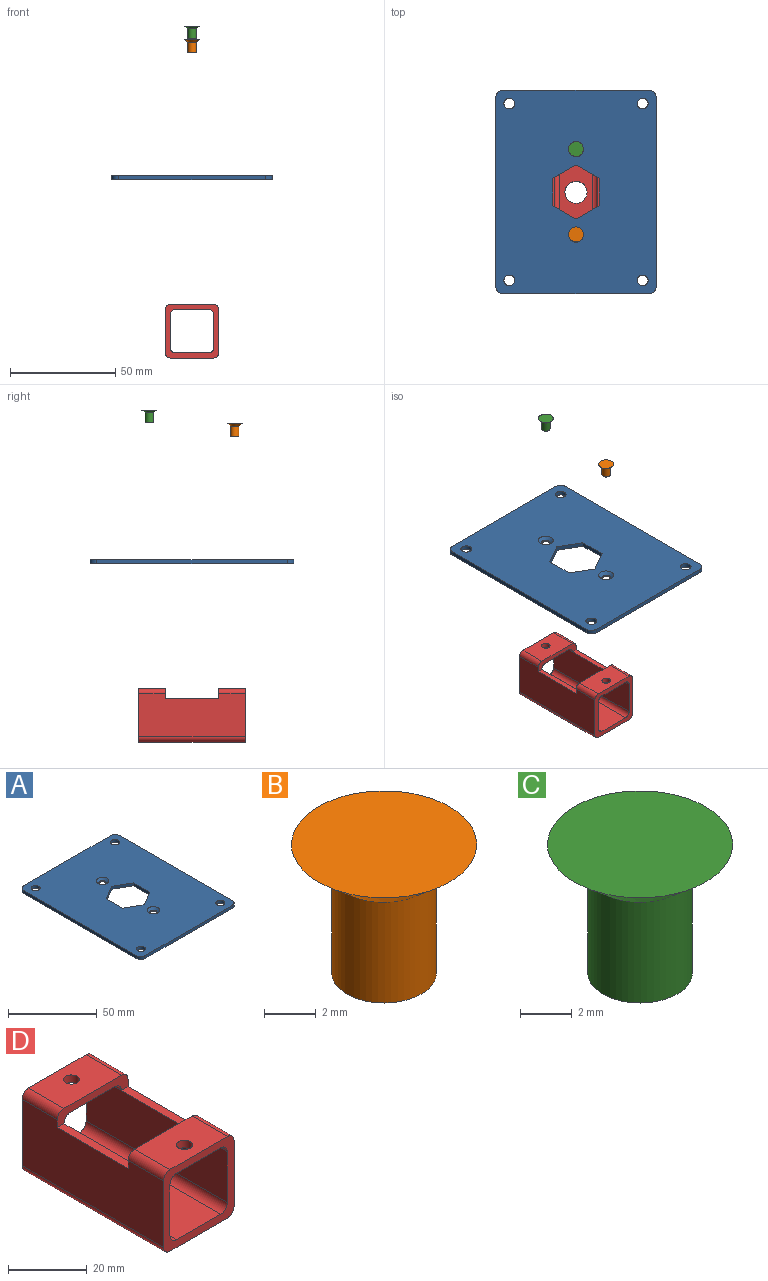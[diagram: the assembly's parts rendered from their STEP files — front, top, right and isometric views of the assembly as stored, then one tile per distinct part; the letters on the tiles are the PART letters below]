
ASSEMBLY  parts=4 mates=3
PART A: 24 faces, bbox 76.2x96.8x2 mm
  f0: plane 11.11x6.42mm, normal (0.5,-0.87,0), area 26.1mm2, adj f1,f13,f14,f15
  f1: plane 11.11x6.42mm, normal (-0.5,-0.87,0), area 26.1mm2, adj f0,f2,f14,f15
  f2: plane 12.83x2.03mm, normal (-1,0,0), area 26.1mm2, adj f1,f3,f14,f15
  f3: plane 11.11x6.42mm, normal (-0.5,0.87,0), area 26.1mm2, adj f2,f4,f14,f15
  f4: plane 11.11x6.42mm, normal (0.5,0.87,0), area 26.1mm2, adj f3,f13,f14,f15
  f5: plane 90.49x2.03mm, normal (1,0,0), area 183.9mm2, adj f6,f12,f14,f15
  f6: cylinder r=3.17mm len=3.18mm, axis (0,0,-1), area 10.1mm2, adj f5,f7,f14,f15
  f7: plane 69.85x2.03mm, normal (0,1,0), area 141.9mm2, adj f6,f8,f14,f15
  f8: cylinder r=3.17mm len=3.18mm, axis (0,0,-1), area 10.1mm2, adj f7,f9,f14,f15
  f9: plane 90.49x2.03mm, normal (-1,0,0), area 183.9mm2, adj f8,f10,f14,f15
  f10: cylinder r=3.17mm len=3.18mm, axis (0,0,-1), area 10.1mm2, adj f9,f11,f14,f15
  f11: plane 69.85x2.03mm, normal (0,-1,0), area 141.9mm2, adj f10,f12,f14,f15
  f12: cylinder r=3.17mm len=3.18mm, axis (0,0,-1), area 10.1mm2, adj f5,f11,f14,f15
  f13: plane 12.83x2.03mm, normal (1,0,0), area 26.1mm2, adj f0,f4,f14,f15
  f14: plane 96.84x76.2mm, normal (0,0,1), area 6780.5mm2, adj f0,f1,f2,f3,f4,f5,f6,f7
  f15: plane 96.84x76.2mm, normal (0,0,-1), area 6835.1mm2, adj f0,f1,f2,f3,f4,f5,f6,f7
  f16: cylinder r=2.55mm len=5.11mm, axis (0,0,-1), area 32.6mm2, adj f14,f15
  f17: cylinder r=2.55mm len=5.11mm, axis (0,0,-1), area 32.6mm2, adj f14,f15
  f18: cylinder r=2.55mm len=5.11mm, axis (0,0,-1), area 32.6mm2, adj f14,f15
  f19: cylinder r=2.55mm len=5.11mm, axis (0,0,-1), area 32.6mm2, adj f14,f15
  f20: cylinder r=2.02mm len=4.04mm, axis (0,0,1), area 9.3mm2, adj f15,f21
  f21: cone r=2.02mm half-angle=50deg, axis (0,0,1), area 35.6mm2, adj f14,f20
  f22: cylinder r=2.02mm len=4.04mm, axis (0,0,1), area 9.3mm2, adj f15,f23
  f23: cone r=2.02mm half-angle=50deg, axis (0,0,1), area 35.6mm2, adj f14,f22
PART B: 4 faces, bbox 7.1x7.1x6.1 mm
  f0: plane 7.14x7.14mm, normal (0,0,1), area 40.1mm2, adj f1
  f1: cone r=3.57mm half-angle=50deg, axis (0,0,1), area 35.6mm2, adj f0,f2
  f2: cylinder r=2.02mm len=4.76mm, axis (0,0,1), area 60.4mm2, adj f1,f3
  f3: plane 4.04x4.04mm, normal (0,0,-1), area 12.8mm2, adj f2
PART C: 4 faces, bbox 7.1x7.1x6.1 mm
  f0: plane 7.14x7.14mm, normal (0,0,1), area 40.1mm2, adj f1
  f1: cone r=3.57mm half-angle=50deg, axis (0,0,1), area 35.6mm2, adj f0,f2
  f2: cylinder r=2.02mm len=4.76mm, axis (0,0,1), area 60.4mm2, adj f1,f3
  f3: plane 4.04x4.04mm, normal (0,0,-1), area 12.8mm2, adj f2
PART D: 31 faces, bbox 25.4x50.8x25.4 mm
  f0: plane 20.64x12.7mm, normal (0,0,1), area 249.3mm2, adj f7,f9,f23,f25,f26
  f1: cylinder r=2.38mm len=12.7mm, axis (0,1,0), area 47.5mm2, adj f6,f8,f22,f27
  f2: cylinder r=2.38mm len=12.7mm, axis (0,1,0), area 47.5mm2, adj f8,f10,f22,f27
  f3: cylinder r=2.38mm len=12.7mm, axis (0,1,0), area 47.5mm2, adj f4,f17,f22,f27
  f4: plane 15.88x12.7mm, normal (0,0,-1), area 188.8mm2, adj f3,f5,f22,f24,f27
  f5: cylinder r=2.38mm len=12.7mm, axis (0,1,0), area 47.5mm2, adj f4,f21,f22,f27
  f6: plane 50.8x20.64mm, normal (1,0,0), area 987.9mm2, adj f1,f7,f13,f22,f23,f26,f27,f28
  f7: cylinder r=2.38mm len=12.7mm, axis (0,1,0), area 47.5mm2, adj f0,f6,f23,f26
  f8: plane 20.64x12.7mm, normal (0,0,1), area 249.3mm2, adj f1,f2,f22,f24,f27
  f9: cylinder r=2.38mm len=12.7mm, axis (0,1,0), area 47.5mm2, adj f0,f10,f23,f26
  f10: plane 50.8x20.64mm, normal (-1,0,0), area 987.9mm2, adj f2,f9,f11,f22,f23,f26,f27,f29
  f11: cylinder r=2.38mm len=50.8mm, axis (0,1,0), area 190mm2, adj f10,f12,f22,f23
  f12: plane 50.8x20.64mm, normal (0,0,-1), area 962mm2, adj f11,f13,f22,f23,f30
  f13: cylinder r=2.38mm len=50.8mm, axis (0,1,0), area 190mm2, adj f6,f12,f22,f23
  f14: cylinder r=2.38mm len=50.8mm, axis (0,1,0), area 190mm2, adj f15,f21,f22,f23
  f15: plane 50.8x15.88mm, normal (0,0,1), area 720mm2, adj f14,f16,f22,f23,f30
  f16: cylinder r=2.38mm len=50.8mm, axis (0,1,0), area 190mm2, adj f15,f17,f22,f23
  f17: plane 50.8x15.88mm, normal (1,0,0), area 806.5mm2, adj f3,f16,f18,f22,f23,f29
  f18: cylinder r=2.38mm len=12.7mm, axis (0,1,0), area 47.5mm2, adj f17,f19,f23,f26
  f19: plane 15.88x12.7mm, normal (0,0,-1), area 188.8mm2, adj f18,f20,f23,f25,f26
  f20: cylinder r=2.38mm len=12.7mm, axis (0,1,0), area 47.5mm2, adj f19,f21,f23,f26
  f21: plane 50.8x15.88mm, normal (-1,0,0), area 806.5mm2, adj f5,f14,f20,f22,f23,f28
  f22: plane 25.4x25.4mm, normal (0,-1,0), area 219.3mm2, adj f1,f2,f3,f4,f5,f6,f8,f10
  f23: plane 25.4x25.4mm, normal (0,1,0), area 219.3mm2, adj f0,f6,f7,f9,f10,f11,f12,f13
  f24: cylinder r=2.02mm len=4.04mm, axis (0,0,1), area 30.2mm2, adj f4,f8
  f25: cylinder r=2.02mm len=4.04mm, axis (0,0,1), area 30.2mm2, adj f0,f19
  f26: plane 25.4x4.76mm, normal (0,-1,0), area 71.8mm2, adj f0,f6,f7,f9,f10,f18,f19,f20
  f27: plane 25.4x4.76mm, normal (0,1,0), area 71.8mm2, adj f1,f2,f3,f4,f5,f6,f8,f10
  f28: plane 25.4x2.38mm, normal (0,0,1), area 60.5mm2, adj f6,f21,f26,f27
  f29: plane 25.4x2.38mm, normal (0,0,1), area 60.5mm2, adj f10,f17,f26,f27
  f30: cylinder r=5.25mm len=10.49mm, axis (0,0,1), area 78.5mm2, adj f12,f15
PLACE A at identity fixed
PLACE B t=(0,0,64.77)mm
PLACE C t=(0,0,71.15)mm
PLACE D t=(0,0,-59.41)mm
MATE slider D.f30 <-> A.f15  axis (0,0,-1) through (0,0,-84.81)mm
MATE slider B.f1 <-> A.f22  axis (0,0,1) through (0,-20.32,66.8)mm
MATE slider C.f1 <-> A.f20  axis (0,0,1) through (0,20.32,73.18)mm
